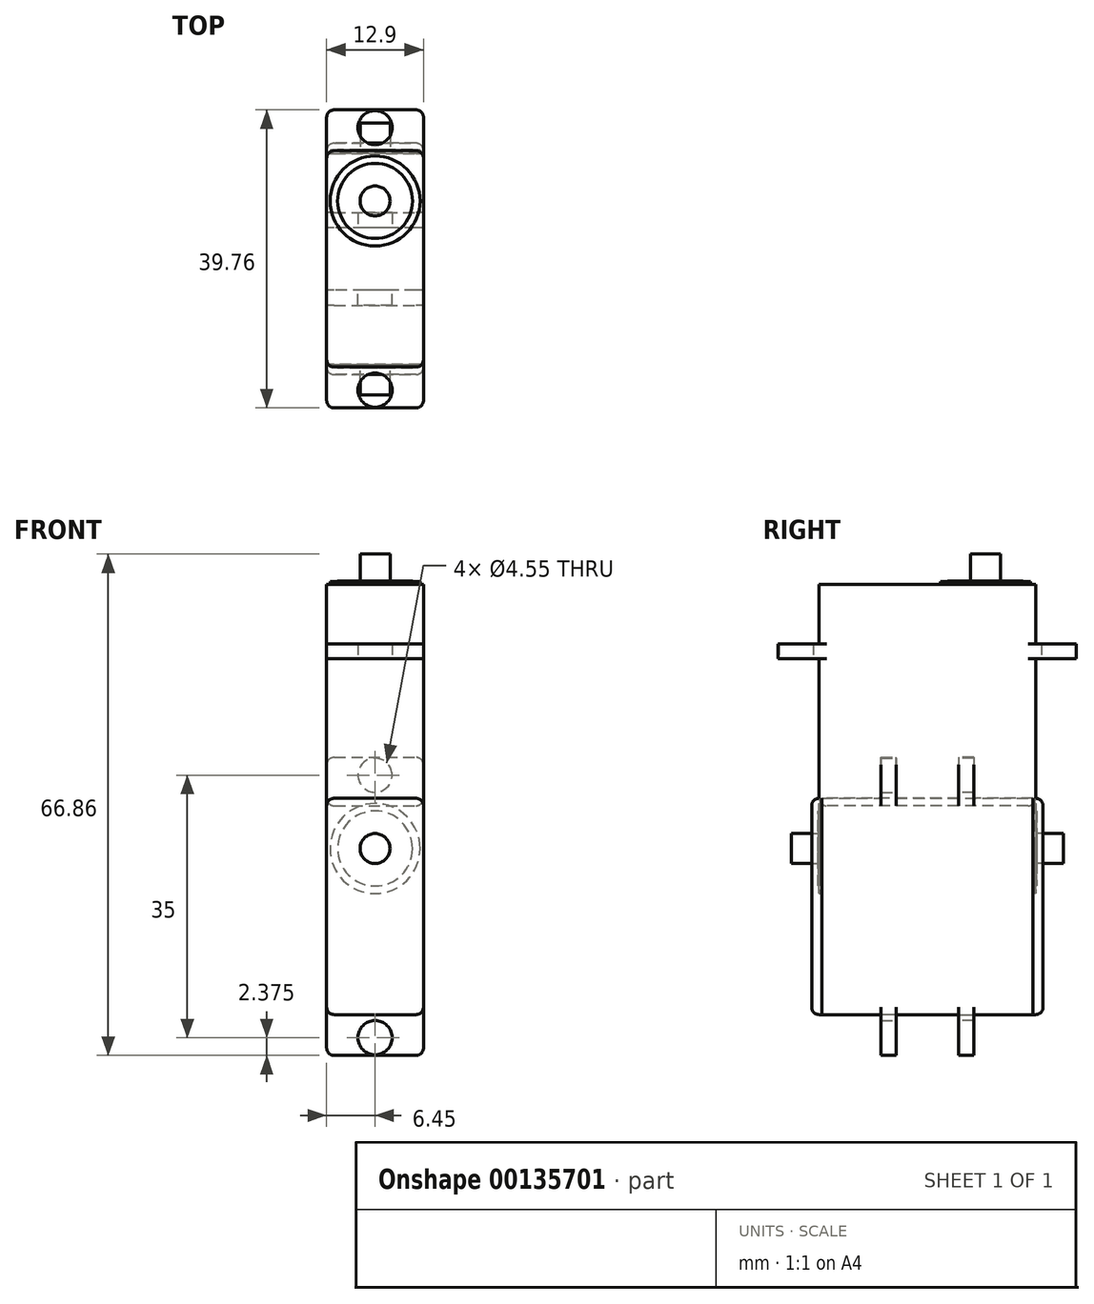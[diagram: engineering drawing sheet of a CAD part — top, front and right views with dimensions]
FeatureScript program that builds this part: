
annotation { "Feature Type Name" : "Feature", "Feature Type Description" : "" }
export const myFeature = defineFeature(function(context is Context, id is Id, definition is map)
    precondition{}
    {
        {
            var Q0;
            Q0=qCreatedBy(makeId("Top.planeOp"),FACE);
            var sketch = newSketch(context, id + "F0", { "sketchPlane" : qUnion([Q0])});
            skLineSegment(sketch, "E0.bottom", {"start": v(-6.45, 19.87) * mm, "end": v(6.45, 19.87) * mm});
            skLineSegment(sketch, "E0.top", {"start": v(-6.45, -19.88) * mm, "end": v(6.45, -19.88) * mm});
            skLineSegment(sketch, "E0.left", {"start": v(-6.45, 19.87) * mm, "end": v(-6.45, -19.88) * mm});
            skLineSegment(sketch, "E0.right", {"start": v(6.45, 19.87) * mm, "end": v(6.45, -19.88) * mm});
            skPoint(sketch, "E0.middle", {"position": v(0, 0) * mm});
            skLineSegment(sketch, "E1", {"start": v(-6.45, 14.43) * mm, "end": v(6.45, 14.43) * mm});
            skLineSegment(sketch, "E2", {"start": v(6.45, -14.43) * mm, "end": v(-6.45, -14.43) * mm});
            skCircle(sketch, "E3", {"center": v(0, 17.5) * mm, "radius": 2.27 * mm});
            skCircle(sketch, "E4", {"center": v(0, -17.5) * mm, "radius": 2.27 * mm});
            skSolve(sketch);
        }
        {
            var Q0;
            {var subQ0=sQuery(id+"F0.wireOp",EDGE,"E1");Q0=makeQuery(id+"F0.imprint","IMPRINT",FACE,{"disambiguationData":[TD([[makeQuery(id+"F0.imprint","IMPRINT",EDGE,{"derivedFrom":subQ0}),-1.0]])]});}
            extrude(context, id + "F1", {"entities" : qUnion([Q0]), "depth" : 9.9 * mm});
        }
        {
            var Q0;
            {var subQ0=sQuery(id+"F0.wireOp",EDGE,"E1");Q0=makeQuery(id+"F0.imprint","IMPRINT",FACE,{"disambiguationData":[TD([[makeQuery(id+"F0.imprint","IMPRINT",EDGE,{"derivedFrom":subQ0}),-1.0]])]});}
            extrude(context, id + "F2", {"entities" : qUnion([Q0]), "operationType" : NewBodyOperationType.ADD, "oppositeDirection" : true, "depth" : 19.6 * mm});
        }
        {
            var Q0;
            {var subQ0=sQuery(id+"F0.wireOp",EDGE,"E0.top");Q0=makeQuery(id+"F0.imprint","IMPRINT",FACE,{"disambiguationData":[TD([[makeQuery(id+"F0.imprint","IMPRINT",EDGE,{"derivedFrom":subQ0}),1.0]])]});}
            var Q1;
            {var subQ0=sQuery(id+"F0.wireOp",EDGE,"E0.bottom");Q1=makeQuery(id+"F0.imprint","IMPRINT",FACE,{"disambiguationData":[TD([[makeQuery(id+"F0.imprint","IMPRINT",EDGE,{"derivedFrom":subQ0}),-1.0]])]});}
            extrude(context, id + "F3", {"entities" : qUnion([Q0, Q1]), "operationType" : NewBodyOperationType.ADD, "depth" : 2 * mm});
        }
        {
            var Q0;
            Q0=makeQuery(id+"F1.opExtrude","CAP_FACE",FACE,{"disambiguationData":[OSD([sQuery(id+"F0.wireOp",EDGE,"E0.left"),sQuery(id+"F0.wireOp",EDGE,"E0.right"),sQuery(id+"F0.wireOp",EDGE,"E1"),sQuery(id+"F0.wireOp",EDGE,"E2")])],"isStart":false});
            var sketch = newSketch(context, id + "F4", { "sketchPlane" : qUnion([Q0])});
            skCircle(sketch, "E5", {"center": v(0, 7.73) * mm, "radius": 6 * mm});
            skCircle(sketch, "E6", {"center": v(0, 7.73) * mm, "radius": 5 * mm});
            skSolve(sketch);
        }
        {
            var Q0;
            Q0=makeQuery(id+"F4.imprint","IMPRINT",FACE,{"disambiguationData":[TD([[makeQuery(id+"F4.imprint","IMPRINT",EDGE,{"derivedFrom":sQuery(id+"F4.wireOp",EDGE,"E5")}),1.0]])]});
            extrude(context, id + "F5", {"entities" : qUnion([Q0]), "operationType" : NewBodyOperationType.ADD, "depth" : .4 * mm});
        }
        {
            var Q0;
            Q0=makeQuery(id+"F5.boolean.opBoolean","SPLIT",FACE,{"disambiguationData":[TD([makeQuery(id+"F5.opExtrude","SWEPT_FACE",FACE,{"disambiguationData":[OSD([sQuery(id+"F4.wireOp",EDGE,"E6")])]})])],"derivedFrom":makeQuery(id+"F1.opExtrude","CAP_FACE",FACE,{"disambiguationData":[OSD([sQuery(id+"F0.wireOp",EDGE,"E0.left"),sQuery(id+"F0.wireOp",EDGE,"E0.right"),sQuery(id+"F0.wireOp",EDGE,"E1"),sQuery(id+"F0.wireOp",EDGE,"E2")])],"isStart":false})});
            extrude(context, id + "F6", {"entities" : qUnion([Q0]), "operationType" : NewBodyOperationType.ADD, "depth" : .5 * mm});
        }
        {
            var Q0;
            Q0=makeQuery(id+"F6.opExtrude","CAP_FACE",FACE,{"disambiguationData":[OSD([sQuery(id+"F0.wireOp",EDGE,"E0.left"),sQuery(id+"F0.wireOp",EDGE,"E0.right"),sQuery(id+"F0.wireOp",EDGE,"E1"),sQuery(id+"F0.wireOp",EDGE,"E2")])],"isStart":false});
            var sketch = newSketch(context, id + "F7", { "sketchPlane" : qUnion([Q0])});
            skCircle(sketch, "E7", {"center": v(0, 7.73) * mm, "radius": 2 * mm});
            skSolve(sketch);
        }
        {
            var Q0;
            Q0=makeQuery(id+"F7.imprint","IMPRINT",FACE,{"disambiguationData":[TD([[makeQuery(id+"F7.imprint","IMPRINT",EDGE,{"derivedFrom":sQuery(id+"F7.wireOp",EDGE,"E7")}),1.0]])]});
            extrude(context, id + "F8", {"entities" : qUnion([Q0]), "operationType" : NewBodyOperationType.ADD, "depth" : 3.56 * mm});
        }
        {
            var Q0;
            {var subQ0=sQuery(id+"F0.wireOp",EDGE,"E2");var subQ1=sQuery(id+"F0.wireOp",EDGE,"E1");var subQ2=sQuery(id+"F0.wireOp",EDGE,"E0.right");var subQ3=sQuery(id+"F0.wireOp",EDGE,"E0.left");Q0=makeQuery(id+"F3.boolean.opBoolean","SPLIT",EDGE,{"disambiguationData":[TD([makeQuery(id+"F2.opExtrude","CAP_FACE",FACE,{"disambiguationData":[OSD([subQ3,subQ2,subQ1,subQ0])],"isStart":false})])],"derivedFrom":makeQuery(id+"F2.boolean.opBoolean","MERGE",EDGE,{"derivedFrom":[makeQuery(id+"F1.opExtrude","SWEPT_EDGE",EDGE,{"disambiguationData":[OSD([subQ3,subQ0])]}),makeQuery(id+"F2.opExtrude","SWEPT_EDGE",EDGE,{"disambiguationData":[OSD([subQ3,subQ0])]})]})});}
            var Q1;
            {var subQ0=sQuery(id+"F0.wireOp",EDGE,"E0.left");var subQ2=sQuery(id+"F0.wireOp",EDGE,"E2");var subQ3=sQuery(id+"F0.wireOp",EDGE,"E1");var subQ4=sQuery(id+"F0.wireOp",EDGE,"E0.right");Q1=makeQuery(id+"F3.boolean.opBoolean","SPLIT",EDGE,{"disambiguationData":[TD([makeQuery(id+"F1.opExtrude","CAP_FACE",FACE,{"disambiguationData":[OSD([subQ0,subQ4,subQ3,subQ2])],"isStart":false})])],"derivedFrom":makeQuery(id+"F2.boolean.opBoolean","MERGE",EDGE,{"derivedFrom":[makeQuery(id+"F1.opExtrude","SWEPT_EDGE",EDGE,{"disambiguationData":[OSD([subQ0,subQ2])]}),makeQuery(id+"F2.opExtrude","SWEPT_EDGE",EDGE,{"disambiguationData":[OSD([subQ0,subQ2])]})]})});}
            var Q2;
            {var subQ0=sQuery(id+"F0.wireOp",EDGE,"E0.right");var subQ1=sQuery(id+"F0.wireOp",EDGE,"E2");var subQ3=sQuery(id+"F0.wireOp",EDGE,"E1");var subQ4=sQuery(id+"F0.wireOp",EDGE,"E0.left");Q2=makeQuery(id+"F3.boolean.opBoolean","SPLIT",EDGE,{"disambiguationData":[TD([makeQuery(id+"F1.opExtrude","CAP_FACE",FACE,{"disambiguationData":[OSD([subQ4,subQ0,subQ3,subQ1])],"isStart":false})])],"derivedFrom":makeQuery(id+"F2.boolean.opBoolean","MERGE",EDGE,{"derivedFrom":[makeQuery(id+"F1.opExtrude","SWEPT_EDGE",EDGE,{"disambiguationData":[OSD([subQ0,subQ1])]}),makeQuery(id+"F2.opExtrude","SWEPT_EDGE",EDGE,{"disambiguationData":[OSD([subQ0,subQ1])]})]})});}
            var Q3;
            {var subQ0=sQuery(id+"F0.wireOp",EDGE,"E0.right");var subQ1=sQuery(id+"F0.wireOp",EDGE,"E2");var subQ2=sQuery(id+"F0.wireOp",EDGE,"E1");var subQ3=sQuery(id+"F0.wireOp",EDGE,"E0.left");Q3=makeQuery(id+"F3.boolean.opBoolean","SPLIT",EDGE,{"disambiguationData":[TD([makeQuery(id+"F2.opExtrude","CAP_FACE",FACE,{"disambiguationData":[OSD([subQ3,subQ0,subQ2,subQ1])],"isStart":false})])],"derivedFrom":makeQuery(id+"F2.boolean.opBoolean","MERGE",EDGE,{"derivedFrom":[makeQuery(id+"F1.opExtrude","SWEPT_EDGE",EDGE,{"disambiguationData":[OSD([subQ0,subQ1])]}),makeQuery(id+"F2.opExtrude","SWEPT_EDGE",EDGE,{"disambiguationData":[OSD([subQ0,subQ1])]})]})});}
            var Q4;
            Q4=makeQuery(id+"F2.opExtrude","CAP_EDGE",EDGE,{"disambiguationData":[OSD([sQuery(id+"F0.wireOp",EDGE,"E2")])],"isStart":false});
            var Q5;
            Q5=makeQuery(id+"F2.opExtrude","CAP_EDGE",EDGE,{"disambiguationData":[OSD([sQuery(id+"F0.wireOp",EDGE,"E0.left")])],"isStart":false});
            var Q6;
            {var subQ0=sQuery(id+"F0.wireOp",EDGE,"E2");var subQ1=sQuery(id+"F0.wireOp",EDGE,"E1");var subQ2=sQuery(id+"F0.wireOp",EDGE,"E0.right");var subQ3=sQuery(id+"F0.wireOp",EDGE,"E0.left");Q6=makeQuery(id+"F3.boolean.opBoolean","SPLIT",EDGE,{"disambiguationData":[TD([makeQuery(id+"F2.opExtrude","CAP_FACE",FACE,{"disambiguationData":[OSD([subQ3,subQ2,subQ1,subQ0])],"isStart":false})])],"derivedFrom":makeQuery(id+"F2.boolean.opBoolean","MERGE",EDGE,{"derivedFrom":[makeQuery(id+"F1.opExtrude","SWEPT_EDGE",EDGE,{"disambiguationData":[OSD([subQ3,subQ1])]}),makeQuery(id+"F2.opExtrude","SWEPT_EDGE",EDGE,{"disambiguationData":[OSD([subQ3,subQ1])]})]})});}
            var Q7;
            {var subQ0=sQuery(id+"F0.wireOp",EDGE,"E0.left");var subQ1=sQuery(id+"F0.wireOp",EDGE,"E2");var subQ2=sQuery(id+"F0.wireOp",EDGE,"E1");var subQ3=sQuery(id+"F0.wireOp",EDGE,"E0.right");Q7=makeQuery(id+"F3.boolean.opBoolean","SPLIT",EDGE,{"disambiguationData":[TD([makeQuery(id+"F1.opExtrude","CAP_FACE",FACE,{"disambiguationData":[OSD([subQ0,subQ3,subQ2,subQ1])],"isStart":false})])],"derivedFrom":makeQuery(id+"F2.boolean.opBoolean","MERGE",EDGE,{"derivedFrom":[makeQuery(id+"F1.opExtrude","SWEPT_EDGE",EDGE,{"disambiguationData":[OSD([subQ0,subQ2])]}),makeQuery(id+"F2.opExtrude","SWEPT_EDGE",EDGE,{"disambiguationData":[OSD([subQ0,subQ2])]})]})});}
            var Q8;
            Q8=makeQuery(id+"F2.opExtrude","CAP_EDGE",EDGE,{"disambiguationData":[OSD([sQuery(id+"F0.wireOp",EDGE,"E1")])],"isStart":false});
            var Q9;
            {var subQ0=sQuery(id+"F0.wireOp",EDGE,"E0.right");var subQ1=sQuery(id+"F0.wireOp",EDGE,"E1");var subQ2=sQuery(id+"F0.wireOp",EDGE,"E0.left");var subQ4=sQuery(id+"F0.wireOp",EDGE,"E2");Q9=makeQuery(id+"F3.boolean.opBoolean","SPLIT",EDGE,{"disambiguationData":[TD([makeQuery(id+"F2.opExtrude","CAP_FACE",FACE,{"disambiguationData":[OSD([subQ2,subQ0,subQ1,subQ4])],"isStart":false})])],"derivedFrom":makeQuery(id+"F2.boolean.opBoolean","MERGE",EDGE,{"derivedFrom":[makeQuery(id+"F1.opExtrude","SWEPT_EDGE",EDGE,{"disambiguationData":[OSD([subQ0,subQ1])]}),makeQuery(id+"F2.opExtrude","SWEPT_EDGE",EDGE,{"disambiguationData":[OSD([subQ0,subQ1])]})]})});}
            var Q10;
            {var subQ0=sQuery(id+"F0.wireOp",EDGE,"E0.right");var subQ1=sQuery(id+"F0.wireOp",EDGE,"E1");var subQ2=sQuery(id+"F0.wireOp",EDGE,"E2");var subQ3=sQuery(id+"F0.wireOp",EDGE,"E0.left");Q10=makeQuery(id+"F3.boolean.opBoolean","SPLIT",EDGE,{"disambiguationData":[TD([makeQuery(id+"F1.opExtrude","CAP_FACE",FACE,{"disambiguationData":[OSD([subQ3,subQ0,subQ1,subQ2])],"isStart":false})])],"derivedFrom":makeQuery(id+"F2.boolean.opBoolean","MERGE",EDGE,{"derivedFrom":[makeQuery(id+"F1.opExtrude","SWEPT_EDGE",EDGE,{"disambiguationData":[OSD([subQ0,subQ1])]}),makeQuery(id+"F2.opExtrude","SWEPT_EDGE",EDGE,{"disambiguationData":[OSD([subQ0,subQ1])]})]})});}
            var Q11;
            Q11=makeQuery(id+"F2.opExtrude","CAP_EDGE",EDGE,{"disambiguationData":[OSD([sQuery(id+"F0.wireOp",EDGE,"E0.right")])],"isStart":false});
            var Q12;
            Q12=makeQuery(id+"F3.opExtrude","SWEPT_EDGE",EDGE,{"disambiguationData":[OSD([sQuery(id+"F0.wireOp",EDGE,"E0.bottom"),sQuery(id+"F0.wireOp",EDGE,"E0.left")])]});
            var Q13;
            Q13=makeQuery(id+"F3.opExtrude","SWEPT_EDGE",EDGE,{"disambiguationData":[OSD([sQuery(id+"F0.wireOp",EDGE,"E0.bottom"),sQuery(id+"F0.wireOp",EDGE,"E0.right")])]});
            var Q14;
            Q14=makeQuery(id+"F3.opExtrude","SWEPT_EDGE",EDGE,{"disambiguationData":[OSD([sQuery(id+"F0.wireOp",EDGE,"E0.top"),sQuery(id+"F0.wireOp",EDGE,"E0.left")])]});
            var Q15;
            Q15=makeQuery(id+"F3.opExtrude","SWEPT_EDGE",EDGE,{"disambiguationData":[OSD([sQuery(id+"F0.wireOp",EDGE,"E0.top"),sQuery(id+"F0.wireOp",EDGE,"E0.right")])]});
            fillet(context, id + "F9", {"entities" : qUnion([Q0, Q1, Q2, Q3, Q4, Q5, Q6, Q7, Q8, Q9, Q10, Q11, Q12, Q13, Q14, Q15]), "radius" : 1 * mm, "tangentPropagation" : true, "allowEdgeOverflow" : false});
        }
        {
            var Q0;
            Q0=makeQuery(id+"F1.opExtrude","SWEPT_BODY",BODY,{"disambiguationData":[OSD([sQuery(id+"F0.wireOp",EDGE,"E0.left"),sQuery(id+"F0.wireOp",EDGE,"E0.right"),sQuery(id+"F0.wireOp",EDGE,"E1"),sQuery(id+"F0.wireOp",EDGE,"E2")])]});
            var Q1;
            {var subQ0=sQuery(id+"F0.wireOp",EDGE,"E2");var subQ1=sQuery(id+"F0.wireOp",EDGE,"E1");var subQ2=sQuery(id+"F0.wireOp",EDGE,"E0.right");var subQ3=sQuery(id+"F0.wireOp",EDGE,"E0.left");Q1=makeQuery(id+"F9.opFillet","BLEND_EDGE",EDGE,{"blendedFrom":[makeQuery(id+"F2.opExtrude","CAP_EDGE",EDGE,{"disambiguationData":[OSD([subQ1])],"isStart":false}),makeQuery(id+"F3.boolean.opBoolean","SPLIT",FACE,{"disambiguationData":[TD([makeQuery(id+"F2.opExtrude","CAP_FACE",FACE,{"disambiguationData":[OSD([subQ3,subQ2,subQ1,subQ0])],"isStart":false})])],"derivedFrom":makeQuery(id+"F2.boolean.opBoolean","MERGE",FACE,{"derivedFrom":[makeQuery(id+"F1.opExtrude","SWEPT_FACE",FACE,{"disambiguationData":[OSD([subQ1])]}),makeQuery(id+"F2.opExtrude","SWEPT_FACE",FACE,{"disambiguationData":[OSD([subQ1])]})]})})],"blendedInto":[makeQuery(id+"F3.boolean.opBoolean","SPLIT",FACE,{"disambiguationData":[TD([makeQuery(id+"F2.opExtrude","CAP_FACE",FACE,{"disambiguationData":[OSD([subQ3,subQ2,subQ1,subQ0])],"isStart":false})])],"derivedFrom":makeQuery(id+"F2.boolean.opBoolean","MERGE",FACE,{"derivedFrom":[makeQuery(id+"F1.opExtrude","SWEPT_FACE",FACE,{"disambiguationData":[OSD([subQ1])]}),makeQuery(id+"F2.opExtrude","SWEPT_FACE",FACE,{"disambiguationData":[OSD([subQ1])]})]})})]});}
            transform(context, id + "F10", {"entities" : qUnion([Q0]), "transformType" : TransformType.ROTATION, "transformAxis" : qUnion([Q1]), "angle" : 90 * degree, "makeCopy" : true});
        }
        {
            var Q0;
            Q0=makeQuery(id+"F10.opPattern","COPY",BODY,{"derivedFrom":makeQuery(id+"F1.opExtrude","SWEPT_BODY",BODY,{"disambiguationData":[OSD([sQuery(id+"F0.wireOp",EDGE,"E0.left"),sQuery(id+"F0.wireOp",EDGE,"E0.right"),sQuery(id+"F0.wireOp",EDGE,"E1"),sQuery(id+"F0.wireOp",EDGE,"E2")])]}),"instanceName":"1"});
            var Q1;
            Q1=qCreatedBy(makeId("Front.planeOp"),FACE);
            mirror(context, id + "F11", {"entities" : qUnion([Q0]), "mirrorPlane" : qUnion([Q1])});
        }
    });
